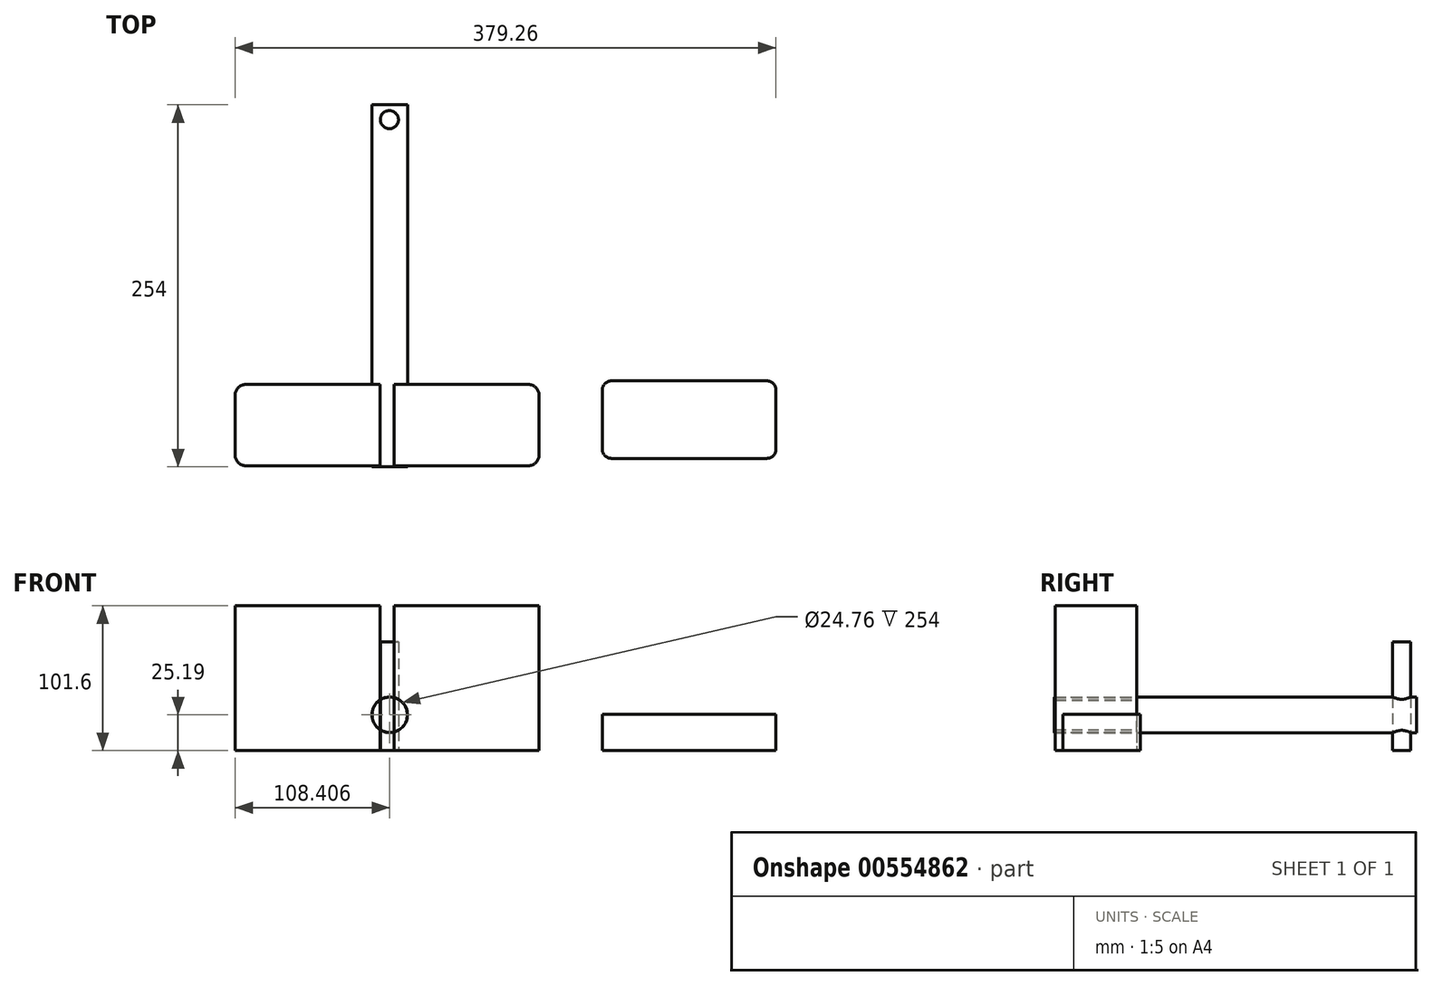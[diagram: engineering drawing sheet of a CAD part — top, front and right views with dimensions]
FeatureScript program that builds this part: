
annotation { "Feature Type Name" : "Feature", "Feature Type Description" : "" }
export const myFeature = defineFeature(function(context is Context, id is Id, definition is map)
    precondition{}
    {
        {
            var Q0;
            Q0=qCreatedBy(makeId("Front.planeOp"),FACE);
            var sketch = newSketch(context, id + "F0", { "sketchPlane" : qUnion([Q0])});
            skCircle(sketch, "E0", {"center": v(-18.72, 25.2) * mm, "radius": 12.38 * mm});
            skCircle(sketch, "E1", {"center": v(-18.72, 25.2) * mm, "radius": 12.5 * mm});
            skSolve(sketch);
        }
        {
            var Q0;
            Q0 = qSketchRegion(id + "F0", true);
            extrude(context, id + "F1", {"entities" : qUnion([Q0]), "depth" : 254 * mm, "offsetDistance" : 25.4 * mm});
        }
        {
            var Q0;
            Q0=qCreatedBy(makeId("Top.planeOp"),FACE);
            var sketch = newSketch(context, id + "F2", { "sketchPlane" : qUnion([Q0])});
            skLineSegment(sketch, "E2.bottom", {"start": v(-25.53, -196.18) * mm, "end": v(-119.5, -196.18) * mm});
            skLineSegment(sketch, "E2.top", {"start": v(-25.53, -253.24) * mm, "end": v(-119.5, -253.24) * mm});
            skLineSegment(sketch, "E2.left", {"start": v(-25.53, -196.18) * mm, "end": v(-25.53, -253.24) * mm});
            skLineSegment(sketch, "E2.right", {"start": v(-127.13, -203.8) * mm, "end": v(-127.13, -245.62) * mm});
            skLineSegment(sketch, "E3.bottom", {"start": v(78.4, -253.24) * mm, "end": v(-15.59, -253.24) * mm});
            skLineSegment(sketch, "E3.top", {"start": v(78.4, -196.18) * mm, "end": v(-15.59, -196.18) * mm});
            skLineSegment(sketch, "E3.left", {"start": v(86.01, -245.62) * mm, "end": v(86.01, -203.8) * mm});
            skLineSegment(sketch, "E3.right", {"start": v(-15.59, -253.24) * mm, "end": v(-15.59, -196.18) * mm});
            skPoint(sketch, "E4.visualSharp", {"position": v(-127.13, -196.18) * mm});
            skArc(sketch, "E4.filletArc", {"start": v(-119.5, -196.18) * mm, "mid": v(-124.9, -198.4) * mm, "end": v(-127.13, -203.8) * mm});
            skPoint(sketch, "E5.visualSharp", {"position": v(-127.13, -253.24) * mm});
            skArc(sketch, "E5.filletArc", {"start": v(-127.13, -245.62) * mm, "mid": v(-124.9, -251.01) * mm, "end": v(-119.5, -253.24) * mm});
            skPoint(sketch, "E6.visualSharp", {"position": v(86.01, -196.18) * mm});
            skArc(sketch, "E6.filletArc", {"start": v(86.01, -203.8) * mm, "mid": v(83.78, -198.4) * mm, "end": v(78.4, -196.18) * mm});
            skPoint(sketch, "E7.visualSharp", {"position": v(86.01, -253.24) * mm});
            skArc(sketch, "E7.filletArc", {"start": v(78.4, -253.24) * mm, "mid": v(83.78, -251.01) * mm, "end": v(86.01, -245.62) * mm});
            skSolve(sketch);
        }
        {
            var Q0;
            Q0=makeQuery(id+"F2.imprint","IMPRINT",FACE,{"disambiguationData":[TD([[makeQuery(id+"F2.imprint","IMPRINT",EDGE,{"derivedFrom":sQuery(id+"F2.wireOp",EDGE,"E2.bottom")}),1.0]])]});
            var Q1;
            Q1 = qSketchRegion(id + "F2", true);
            extrude(context, id + "F3", {"entities" : qUnion([Q0, Q1]), "operationType" : NewBodyOperationType.ADD, "depth" : 101.6 * mm, "offsetDistance" : 25.4 * mm});
        }
        {
            var Q0;
            Q0=qCreatedBy(makeId("Top.planeOp"),FACE);
            var sketch = newSketch(context, id + "F4", { "sketchPlane" : qUnion([Q0])});
            skCircle(sketch, "E8", {"center": v(-18.94, -10.4) * mm, "radius": 6.35 * mm});
            skSolve(sketch);
        }
        {
            var Q0;
            Q0 = qSketchRegion(id + "F4", true);
            extrude(context, id + "F5", {"entities" : qUnion([Q0]), "operationType" : NewBodyOperationType.ADD, "depth" : 76.2 * mm, "offsetDistance" : 25.4 * mm});
        }
        {
            var Q0;
            Q0=qCreatedBy(makeId("Top.planeOp"),FACE);
            var sketch = newSketch(context, id + "F6", { "sketchPlane" : qUnion([Q0])});
            skLineSegment(sketch, "E9.bottom", {"start": v(136.77, -193.67) * mm, "end": v(245.78, -193.67) * mm});
            skLineSegment(sketch, "E9.top", {"start": v(136.77, -248.04) * mm, "end": v(245.78, -248.04) * mm});
            skLineSegment(sketch, "E9.left", {"start": v(130.42, -200.02) * mm, "end": v(130.42, -241.69) * mm});
            skLineSegment(sketch, "E9.right", {"start": v(252.13, -200.02) * mm, "end": v(252.13, -241.69) * mm});
            skLineSegment(sketch, "E10", {"start": v(130.42, -193.67) * mm, "end": v(-6.65, -164.26) * mm});
            skLineSegment(sketch, "E11", {"start": v(252.13, -193.67) * mm, "end": v(-8.85, -127.17) * mm});
            skPoint(sketch, "E12.visualSharp", {"position": v(130.42, -193.67) * mm});
            skArc(sketch, "E12.filletArc", {"start": v(136.77, -193.67) * mm, "mid": v(132.28, -195.53) * mm, "end": v(130.42, -200.02) * mm});
            skPoint(sketch, "E13.visualSharp", {"position": v(252.13, -193.67) * mm});
            skArc(sketch, "E13.filletArc", {"start": v(252.13, -200.02) * mm, "mid": v(250.27, -195.53) * mm, "end": v(245.78, -193.67) * mm});
            skPoint(sketch, "E14.visualSharp", {"position": v(130.42, -248.04) * mm});
            skArc(sketch, "E14.filletArc", {"start": v(130.42, -241.69) * mm, "mid": v(132.28, -246.18) * mm, "end": v(136.77, -248.04) * mm});
            skPoint(sketch, "E15.visualSharp", {"position": v(252.13, -248.04) * mm});
            skArc(sketch, "E15.filletArc", {"start": v(245.78, -248.04) * mm, "mid": v(250.27, -246.18) * mm, "end": v(252.13, -241.69) * mm});
            skLineSegment(sketch, "E16", {"start": v(130.42, -220.85) * mm, "end": v(252.13, -220.85) * mm});
            skLineSegment(sketch, "E17", {"start": v(153.97, -193.67) * mm, "end": v(153.97, -248.04) * mm});
            skLineSegment(sketch, "E18", {"start": v(179.53, -193.67) * mm, "end": v(179.53, -248.04) * mm});
            skLineSegment(sketch, "E19", {"start": v(204.65, -193.67) * mm, "end": v(204.66, -248.04) * mm});
            skLineSegment(sketch, "E20", {"start": v(229.84, -193.67) * mm, "end": v(229.86, -248.04) * mm});
            skSolve(sketch);
        }
        {
            var Q0;
            {var subQ5=sQuery(id+"F6.wireOp",EDGE,"E12.filletArc");Q0=makeQuery(id+"F6.imprint","IMPRINT",FACE,{"disambiguationData":[TD([[makeQuery(id+"F6.imprint","IMPRINT",EDGE,{"derivedFrom":subQ5}),1.0]])]});}
            var Q1;
            {var subQ5=sQuery(id+"F6.wireOp",EDGE,"E14.filletArc");Q1=makeQuery(id+"F6.imprint","IMPRINT",FACE,{"disambiguationData":[TD([[makeQuery(id+"F6.imprint","IMPRINT",EDGE,{"derivedFrom":subQ5}),1.0]])]});}
            var Q2;
            {var subQ5=sQuery(id+"F6.wireOp",EDGE,"E15.filletArc");Q2=makeQuery(id+"F6.imprint","IMPRINT",FACE,{"disambiguationData":[TD([[makeQuery(id+"F6.imprint","IMPRINT",EDGE,{"derivedFrom":subQ5}),1.0]])]});}
            var Q3;
            {var subQ0=sQuery(id+"F6.wireOp",EDGE,"E17");var subQ1=sQuery(id+"F6.wireOp",EDGE,"E9.bottom");var subQ2=makeQuery(id+"F6.imprint","INTERSECT",VERTEX,{"derivedFrom":[subQ1,subQ0]});Q3=makeQuery(id+"F6.imprint","IMPRINT",FACE,{"disambiguationData":[TD([[makeQuery(id+"F6.imprint","IMPRINT",EDGE,{"disambiguationData":[TD([[subQ2,-1.0]])],"derivedFrom":subQ1}),-1.0]])]});}
            var Q4;
            {var subQ0=sQuery(id+"F6.wireOp",EDGE,"E18");var subQ1=sQuery(id+"F6.wireOp",EDGE,"E9.bottom");var subQ2=makeQuery(id+"F6.imprint","INTERSECT",VERTEX,{"derivedFrom":[subQ1,subQ0]});Q4=makeQuery(id+"F6.imprint","IMPRINT",FACE,{"disambiguationData":[TD([[makeQuery(id+"F6.imprint","IMPRINT",EDGE,{"disambiguationData":[TD([[subQ2,-1.0]])],"derivedFrom":subQ1}),-1.0]])]});}
            var Q5;
            {var subQ0=sQuery(id+"F6.wireOp",EDGE,"E17");var subQ1=sQuery(id+"F6.wireOp",EDGE,"E9.top");var subQ2=makeQuery(id+"F6.imprint","INTERSECT",VERTEX,{"derivedFrom":[subQ1,subQ0]});Q5=makeQuery(id+"F6.imprint","IMPRINT",FACE,{"disambiguationData":[TD([[makeQuery(id+"F6.imprint","IMPRINT",EDGE,{"disambiguationData":[TD([[subQ2,-1.0]])],"derivedFrom":subQ1}),1.0]])]});}
            var Q6;
            {var subQ0=sQuery(id+"F6.wireOp",EDGE,"E18");var subQ1=sQuery(id+"F6.wireOp",EDGE,"E9.top");var subQ2=makeQuery(id+"F6.imprint","INTERSECT",VERTEX,{"derivedFrom":[subQ1,subQ0]});Q6=makeQuery(id+"F6.imprint","IMPRINT",FACE,{"disambiguationData":[TD([[makeQuery(id+"F6.imprint","IMPRINT",EDGE,{"disambiguationData":[TD([[subQ2,-1.0]])],"derivedFrom":subQ1}),1.0]])]});}
            var Q7;
            {var subQ0=sQuery(id+"F6.wireOp",EDGE,"E19");var subQ1=sQuery(id+"F6.wireOp",EDGE,"E9.top");var subQ2=makeQuery(id+"F6.imprint","INTERSECT",VERTEX,{"derivedFrom":[subQ1,subQ0]});Q7=makeQuery(id+"F6.imprint","IMPRINT",FACE,{"disambiguationData":[TD([[makeQuery(id+"F6.imprint","IMPRINT",EDGE,{"disambiguationData":[TD([[subQ2,-1.0]])],"derivedFrom":subQ1}),1.0]])]});}
            var Q8;
            {var subQ0=sQuery(id+"F6.wireOp",EDGE,"E19");var subQ1=sQuery(id+"F6.wireOp",EDGE,"E9.bottom");var subQ2=makeQuery(id+"F6.imprint","INTERSECT",VERTEX,{"derivedFrom":[subQ1,subQ0]});Q8=makeQuery(id+"F6.imprint","IMPRINT",FACE,{"disambiguationData":[TD([[makeQuery(id+"F6.imprint","IMPRINT",EDGE,{"disambiguationData":[TD([[subQ2,-1.0]])],"derivedFrom":subQ1}),-1.0]])]});}
            var Q9;
            {var subQ0=sQuery(id+"F6.wireOp",EDGE,"E13.filletArc");Q9=makeQuery(id+"F6.imprint","IMPRINT",FACE,{"disambiguationData":[TD([[makeQuery(id+"F6.imprint","IMPRINT",EDGE,{"derivedFrom":subQ0}),1.0]])]});}
            extrude(context, id + "F7", {"entities" : qUnion([Q0, Q1, Q2, Q3, Q4, Q5, Q6, Q7, Q8, Q9]), "depth" : 25.4 * mm, "offsetDistance" : 25.4 * mm});
        }
    });
